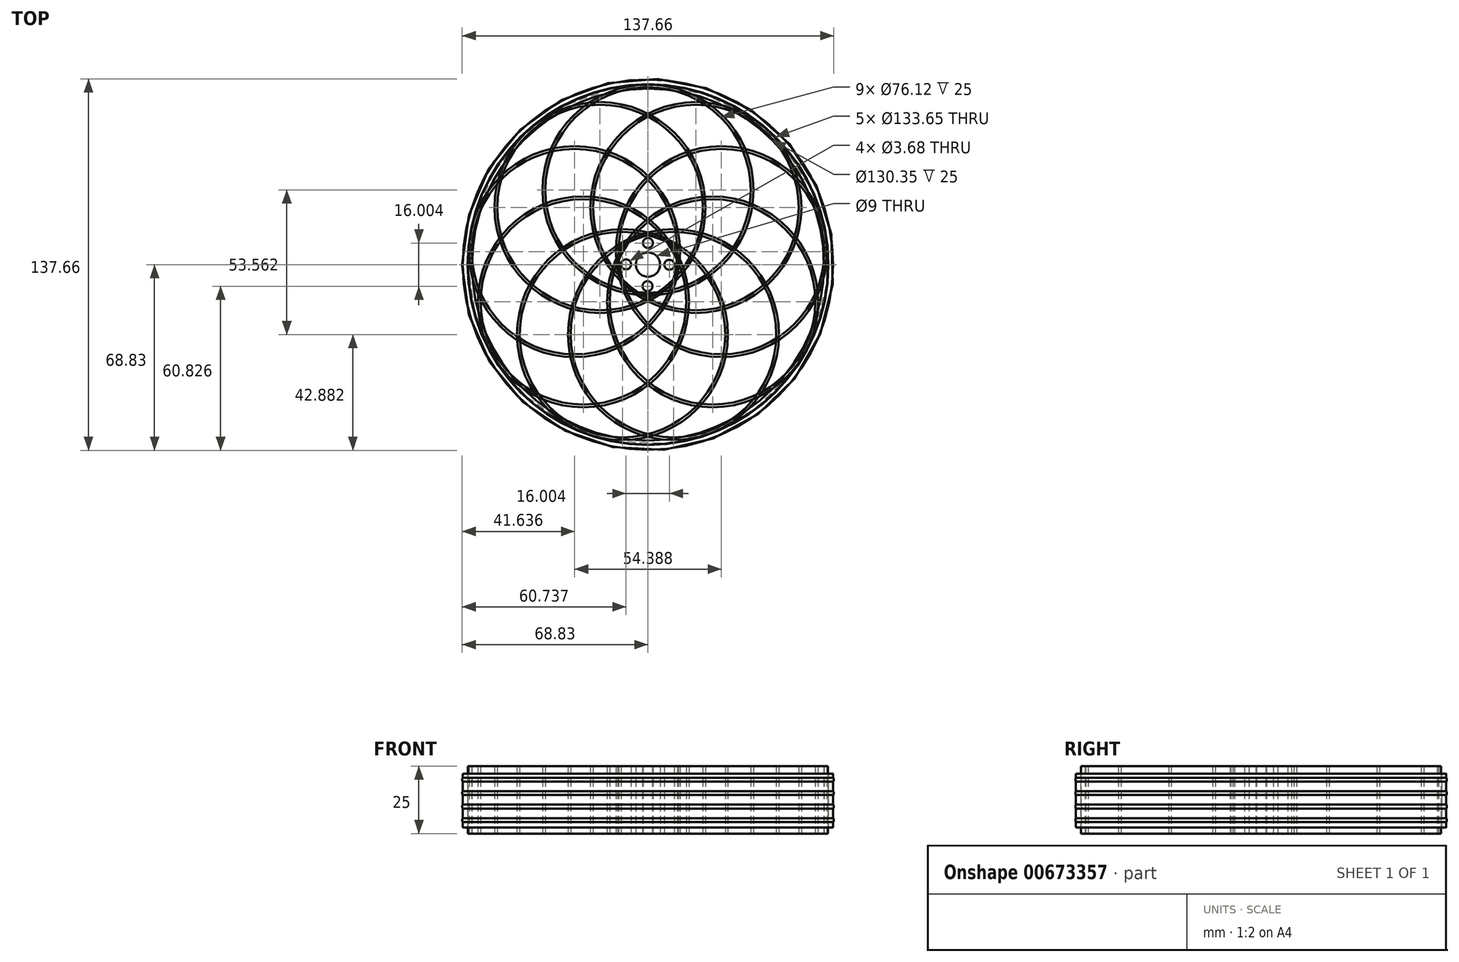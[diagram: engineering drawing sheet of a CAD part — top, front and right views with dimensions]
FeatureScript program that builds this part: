
annotation { "Feature Type Name" : "Feature", "Feature Type Description" : "" }
export const myFeature = defineFeature(function(context is Context, id is Id, definition is map)
    precondition{}
    {
        {
            var Q0;
            Q0=qCreatedBy(makeId("Top.planeOp"),FACE);
            var sketch = newSketch(context, id + "F0", { "sketchPlane" : qUnion([Q0])});
            skCircle(sketch, "E0", {"center": v(0, 0) * mm, "radius": 66.68 * mm});
            skCircle(sketch, "E1.0", {"center": v(0, 0) * mm, "radius": 65.18 * mm});
            skSolve(sketch);
        }
        {
            var Q0;
            Q0=qCreatedBy(makeId("Top.planeOp"),FACE);
            var sketch = newSketch(context, id + "F1", { "sketchPlane" : qUnion([Q0])});
            skPoint(sketch, "E2", {"position": v(0, -11.43) * mm});
            skCircle(sketch, "E3", {"center": v(0, 27.61) * mm, "radius": 39.06 * mm});
            skCircle(sketch, "E4.0", {"center": v(0, 27.61) * mm, "radius": 38.06 * mm});
            skSolve(sketch);
        }
        {
            var Q0;
            Q0=makeQuery(id+"F0.imprint","IMPRINT",FACE,{"disambiguationData":[TD([[makeQuery(id+"F0.imprint","IMPRINT",EDGE,{"derivedFrom":sQuery(id+"F0.wireOp",EDGE,"E0")}),1.0]])]});
            extrude(context, id + "F2", {"entities" : qUnion([Q0]), "depth" : 25 * mm, "offsetDistance" : 25 * mm, "symmetric" : true});
        }
        {
            var Q0;
            Q0=makeQuery(id+"F1.imprint","IMPRINT",FACE,{"disambiguationData":[TD([[makeQuery(id+"F1.imprint","IMPRINT",EDGE,{"derivedFrom":sQuery(id+"F1.wireOp",EDGE,"E3")}),1.0]])]});
            extrude(context, id + "F3", {"entities" : qUnion([Q0]), "depth" : 25 * mm, "offsetDistance" : 25 * mm, "symmetric" : true});
        }
        {
            var Q0;
            Q0=qCreatedBy(makeId("Right.planeOp"),FACE);
            var sketch = newSketch(context, id + "F4", { "sketchPlane" : qUnion([Q0])});
            skLineSegment(sketch, "E5", {"start": v(-11.46, 0) * mm, "end": v(-11.46, 66.16) * mm, "construction": true});
            skLineSegment(sketch, "E6", {"start": v(0, 72.05) * mm, "end": v(0, -72.65) * mm, "construction": true});
            skSolve(sketch);
        }
        {
            var Q0;
            Q0=makeQuery(id+"F3.opExtrude","SWEPT_BODY",BODY,{"disambiguationData":[OSD([sQuery(id+"F1.wireOp",EDGE,"E3"),sQuery(id+"F1.wireOp",EDGE,"E4.0")])]});
            var Q1;
            Q1=sQuery(id+"F4.wireOp",EDGE,"E6");
            circularPattern(context, id + "F5", {"entities" : qUnion([Q0]), "axis" : qUnion([Q1]), "angle" : 360 * degree, "instanceCount" : 9, "equalSpace" : true});
        }
        {
            var Q0;
            Q0=qCreatedBy(makeId("Top.planeOp"),FACE);
            var sketch = newSketch(context, id + "F6", { "sketchPlane" : qUnion([Q0])});
            skCircle(sketch, "E7.0", {"center": v(0, 8) * mm, "radius": 1.84 * mm});
            skCircle(sketch, "E8.0", {"center": v(-8.1, 0.09) * mm, "radius": 1.84 * mm});
            skCircle(sketch, "E9.0", {"center": v(7.91, -0.1) * mm, "radius": 1.84 * mm});
            skCircle(sketch, "E10.0", {"center": v(-0.18, -8) * mm, "radius": 1.84 * mm});
            skCircle(sketch, "E11", {"center": v(0, 0) * mm, "radius": 11.23 * mm});
            skCircle(sketch, "E12", {"center": v(0, 0) * mm, "radius": 4.5 * mm});
            skSolve(sketch);
        }
        {
            var Q0;
            Q0=qSketchRegion(id+"F6",true);
            extrude(context, id + "F7", {"entities" : qUnion([Q0]), "depth" : 25 * mm, "offsetDistance" : 25 * mm, "symmetric" : true});
        }
        {
            var Q0;
            Q0=qCreatedBy(makeId("Front.planeOp"),FACE);
            var sketch = newSketch(context, id + "F8", { "sketchPlane" : qUnion([Q0])});
            skLineSegment(sketch, "E13.bottom", {"start": v(-67.08, -10.27) * mm, "end": v(-68.33, -10.27) * mm});
            skLineSegment(sketch, "E13.top", {"start": v(-67.08, 9.73) * mm, "end": v(-68.33, 9.73) * mm});
            skLineSegment(sketch, "E13.left", {"start": v(-66.83, -10.02) * mm, "end": v(-66.83, 9.48) * mm});
            skLineSegment(sketch, "E13.right", {"start": v(-68.58, -10.02) * mm, "end": v(-68.58, 9.48) * mm});
            skCircle(sketch, "E14", {"center": v(-67.7, 7.48) * mm, "radius": 1.13 * mm});
            skCircle(sketch, "E15.1.0.0", {"center": v(-67.7, 2.48) * mm, "radius": 1.13 * mm});
            skCircle(sketch, "E15.2.0.0", {"center": v(-67.7, -2.52) * mm, "radius": 1.13 * mm});
            skCircle(sketch, "E15.3.0.0", {"center": v(-67.7, -7.52) * mm, "radius": 1.13 * mm});
            skLineSegment(sketch, "E15.direction1", {"start": v(-67.7, 7.48) * mm, "end": v(-67.7, 2.48) * mm, "construction": true});
            skArc(sketch, "E16.filletArc", {"start": v(-68.33, 9.73) * mm, "mid": v(-68.5, 9.66) * mm, "end": v(-68.58, 9.48) * mm});
            skArc(sketch, "E17.filletArc", {"start": v(-66.83, 9.48) * mm, "mid": v(-66.9, 9.66) * mm, "end": v(-67.08, 9.73) * mm});
            skArc(sketch, "E18.filletArc", {"start": v(-67.08, -10.27) * mm, "mid": v(-66.9, -10.2) * mm, "end": v(-66.83, -10.02) * mm});
            skArc(sketch, "E19.filletArc", {"start": v(-68.58, -10.02) * mm, "mid": v(-68.5, -10.2) * mm, "end": v(-68.33, -10.27) * mm});
            skSolve(sketch);
        }
        {
            var Q0;
            Q0=qSketchRegion(id+"F8",true);
            var Q1;
            Q1=sQuery(id+"F0.wireOp",EDGE,"E0");
            revolve(context, id + "F9", {"entities" : qUnion([Q0]), "axis" : qUnion([Q1]), "revolveType" : RevolveType.FULL});
        }
    });
